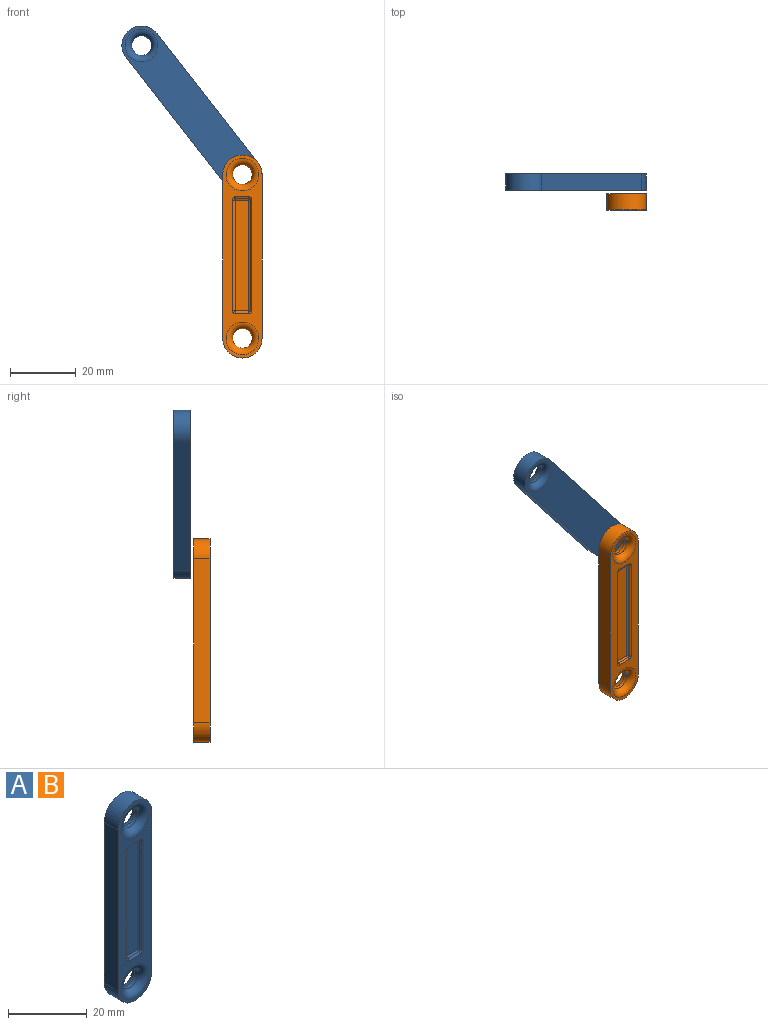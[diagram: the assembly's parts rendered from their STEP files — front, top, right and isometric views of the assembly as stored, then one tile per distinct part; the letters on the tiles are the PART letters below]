
ASSEMBLY  parts=2 mates=1
PART A: 29 faces, bbox 13.9x5x63.9 mm
  f0: plane 62x12mm, normal (0,-1,0), area 341.7mm2, adj f1,f2,f3,f4,f10,f13,f14,f17
  f1: cylinder r=6mm len=12mm, axis (0,1,0), area 94.2mm2, adj f0,f2,f4,f7
  f2: plane 50x5mm, normal (-1,0,0), area 250mm2, adj f0,f1,f3,f7
  f3: cylinder r=6mm len=12mm, axis (0,1,0), area 94.2mm2, adj f0,f2,f4,f7
  f4: plane 50x5mm, normal (1,0,0), area 250mm2, adj f0,f1,f3,f7
  f5: cylinder r=3mm len=6mm, axis (0,1,0), area 18.8mm2, adj f25,f27
  f6: cylinder r=3mm len=6mm, axis (0,1,0), area 18.8mm2, adj f26,f28
  f7: plane 62x12mm, normal (0,1,0), area 556mm2, adj f1,f2,f3,f4,f25,f26
  f8: plane 33.76x4.02mm, normal (0,-1,0), area 135.6mm2, adj f11,f12,f19,f20
  f9: sphere r=0.5mm, area 0.4mm2, adj f10,f11,f12
  f10: torus R=1mm, axis (0,-1,0), area 0.8mm2, adj f0,f9,f13,f14
  f11: cylinder r=0.5mm len=33.76mm, axis (0,0,-1), area 26.5mm2, adj f8,f9,f14,f15
  f12: cylinder r=0.5mm len=4.02mm, axis (-1,0,0), area 3.2mm2, adj f8,f9,f13,f16
  f13: cylinder r=0.5mm len=4.02mm, axis (1,0,0), area 3.2mm2, adj f0,f10,f12,f17
  f14: cylinder r=0.5mm len=33.76mm, axis (0,0,1), area 26.5mm2, adj f0,f10,f11,f18
  f15: sphere r=0.5mm, area 0.4mm2, adj f11,f18,f19
  f16: sphere r=0.5mm, area 0.4mm2, adj f12,f17,f20
  f17: torus R=1mm, axis (0,-1,0), area 0.8mm2, adj f0,f13,f16,f21
  f18: torus R=1mm, axis (0,-1,0), area 0.8mm2, adj f0,f14,f15,f22
  f19: cylinder r=0.5mm len=4.02mm, axis (1,0,0), area 3.2mm2, adj f8,f15,f22,f23
  f20: cylinder r=0.5mm len=33.76mm, axis (0,0,1), area 26.5mm2, adj f8,f16,f21,f23
  f21: cylinder r=0.5mm len=33.76mm, axis (0,0,-1), area 26.5mm2, adj f0,f17,f20,f24
  f22: cylinder r=0.5mm len=4.02mm, axis (-1,0,0), area 3.2mm2, adj f0,f18,f19,f24
  f23: sphere r=0.5mm, area 0.4mm2, adj f19,f20,f24
  f24: torus R=1mm, axis (0,-1,0), area 0.8mm2, adj f0,f21,f22,f23
  f25: torus R=5mm, axis (0,-1,0), area 73.6mm2, adj f5,f7
  f26: torus R=5mm, axis (0,-1,0), area 73.6mm2, adj f6,f7
  f27: torus R=5mm, axis (0,-1,0), area 73.6mm2, adj f0,f5
  f28: torus R=5mm, axis (0,-1,0), area 73.6mm2, adj f0,f6
PART B: same geometry as A
PLACE A rot(axis=(-0.95,0,-0.33),180deg) t=(-15.4,6,19.7)mm
PLACE B t=(0,5,-25)mm
MATE revolute B.f1 <-> A.f1  axis (0,1,0) through (0,5,0)mm
